# Revit family: IS_Linda-X_T4394_BIM_NL
name_source: partatom
category: Plumbing Fixtures
units: mm (PartAtom-declared; Revit-internal decimal feet)

## family parameters
Always vertical = No
Cut with Voids When Loaded = No
OmniClass Number = 23.45.05.14.14
OmniClass Title = Sinks/Lavatories
Part Type = Normal
Room Calculation Point = No
Round Connector Dimension = Use Diameter
Shared = No
Work Plane-Based = No

## types (1)
- T439401 - Linda-X Basin 60cm, 1 Tap Hole, No Overflow - Gloss White
    Accesoires = https://www.idealstandard.nl
    Accessories = https://www.idealstandard.nl
    Afmetingen = 500 x 135 x 600mm
    AfstandsEenheid = Millimeter
    Afwerking = Glänzend weiß
    AreaUnits = Millimeter
    Artikelnummer = T439401
    Artikelomschrijving = Linda-X Waschbecken 60cm, 1 Hahnloch, kein Überlauf
    Artikelreferentie = Linda-X Basin 60cm, 3 Tap Holes, No Overflow
    Auteur = Idea Standard
    BIMObjectName = IS_IdealStandard_Wallhungwashbasins_Linda-X_T4394
    BIMobject category = Sanitary Basins
    BIMobject category code = sanitary-basins
    BIMobject main category = Sanitary
    BIMobject main category code = sanitary
    BarCode = 8014140484875
    Barcode = 8014140484875
    Beschrijvinggarantie = Herstellergarantie
    BimObjectNaam = IS_IdealStandard_Wallhungwashbasins_Linda-X_T4394
    Brand = Idea Standard
    Brand url = http://www.idealstandard.nl
    Breedte = 0
    BrutoGewicht = 0
    Color = Glänzend weiß
    ConnectionType = Plumbing
    Cost = 0 $
    CurrencyUnit = €
    CurrentRevision = 1
    Date of publishing = 14/07/2021
    Description = Linda-X Waschbecken 60cm, 1 Hahnloch, kein Überlauf
    Diepte = 0 mm  [stored 0 ft]
    DurationUnit = Years
    DuurEenheid = Jahre
    Edition number = 1
    Eigenschappen = Waschbecken 60cm, 1 Hahnloch, kein Überlauf
    ElementType = Fixed
    Features = Waschbecken 60cm, 1 Hahnloch, kein Überlauf
    Finish = Glänzend weiß
    GTIN code = https://8014140484875
    Garantieunits = Jahren
    Help = https://www.idealstandard.nl
    Hoogte = 135.00797
    Hulp = https://www.idealstandard.nl
    IFC Classification = Sanitary Terminal
    IfcExportAs = IfcSanitaryTerminalType
    IfcExportType = WASHHANDBASIN
    Installatieinstructies = https://www.idealstandard.nl
    Installation instructions = https://www.idealstandard.nl
    InstallationInstructions = https://www.idealstandard.nl
    Kleur = Glänzend weiß
    Lengte = 500 mm
    LinearUnits = Millimetres
    MainColor = White
    MaintenanceInformation = https://www.idealstandard.nl
    Manufacturer = Ideal Standard
    Manufacturer name = Ideal Standard
    ManufacturerURL = https://www.idealstandard.nl
    Masterformat 2014 Code = 33 44 13.13
    Masterformat 2014 Description = Catchbasins
    Materiaal = Keramik
    Material = Diamatec
    Material main = Keramik
    MaterialThickness = 0 mm  [stored 0 ft]
    Merk = Ideal Standard
    Model = T439401
    ModelNumber = T439401
    ModelReference = Linda-X Basin 60cm, 3 Tap Holes, No Overflow
    Montageinstuctie = https://www.idealstandard.nl
    NBS Reference Code = 45-35-70/369
    NBS Reference Description = Wall hung wash basins
    Name = Wallhungwashbasins_Linda-X_T4394_IdealStandard
    NettWeight = 15.5
    Nettogewicht = 0
    NominalDepth = 500 mm
    NominalHeight = 135 mm  [stored 0.442913 ft]
    NominalWidth = 600 mm
    Normen = Wallhungwashbasins_Linda-X_T4394_IdealStandard
    OmniClass Code = 23-39 29 13 21 19
    OmniClass Description = Surface Water Retention Basins
    Ophangingwastafel = Wand oder Sockel installiert
    OppervlakteEenheid = Millimeter
    OutletConnectionSize = 0 mm  [stored 0 ft]
    Product Guid = ab121cbb-d953-4e58-bd1c-c8d362d5e275
    Product SKU = T4394
    Product certification = https://www.idealstandard.nl
    Product data url = https://bimobject.com
    Product family = Linda-X
    Product group = Washbasins
    Product name = Linda-X Basin 60cm, 1 Tap Hole, No Overflow
    Product url = https://www.idealstandard.nl
    ProductInformation = https://www.idealstandard.nl
    Productinformatie = https://www.idealstandard.nl
    QR code = http://bimobject.com
    Referentie = Linda-X Basin 60cm, 1 Tap Hole, No Overflow
    Revisie = 1
    Shape = Rechteckig
    Size = 500 x 135 x 600mm
    Space = Internal
    SpareParts = https://www.idealstandard.nl
    Technical description = https://www.idealstandard.nl
    Telefoonnummer = 077 355 08 08
    Typeconnectie = Installation
    Typewastafel = Rechteckig, Wand oder Sockel installiert
    UNSPSC Code = 301815
    URL = https://www.idealstandard.nl
    Uniclass 1.4 Code = L7212
    Uniclass 1.4 Description = Washbasins
    Uniclass 2.0 Code = PR-31-79
    Uniclass 2.0 Description = Sinks, Wash Basins And Troughs
    Uniclass 2015 Code = Pr_40_20_96_96
    Uniclass 2015 Name = Wall-hung washbasins
    Uniclass2015Beschrijving = Wall-hung washbasins
    Uniclass2015Code = Pr_40_20_96_96
    Uniclass2015Referentie = Pr_40_20_96_96
    Uniclass2015Title = Wall-hung washbasins
    Uniclass2015Version = v1.20
    Urlproducent = https://www.idealstandard.nl
    ValutaEenheid = €
    Versie = 1
    Version = 1
    Vervangingskosten = 0
    VolumeUnits = Litres
    Volumeunits = Liter
    Vorm = Rechteckig
    WRASURL = https://www.wrasapprovals.co.uk
    WarrantyDescription = Manufacturer Warranty
    WarrantyDurationUnit = 5
    WashHandBasinMounting = Wall Hung
    WashHandBasinType = Wall Hung Wash Basin
    Wisselstukken = https://www.idealstandard.nl
    Youtube clip = https://www.youtube.com

note: [stored X ft] marks values corroborated as IEEE doubles in the binary element streams (Revit-internal decimal feet)

## geometry (parser evidence)
native form markers: Sweep x3
no freeform markers — native parametric forms only
